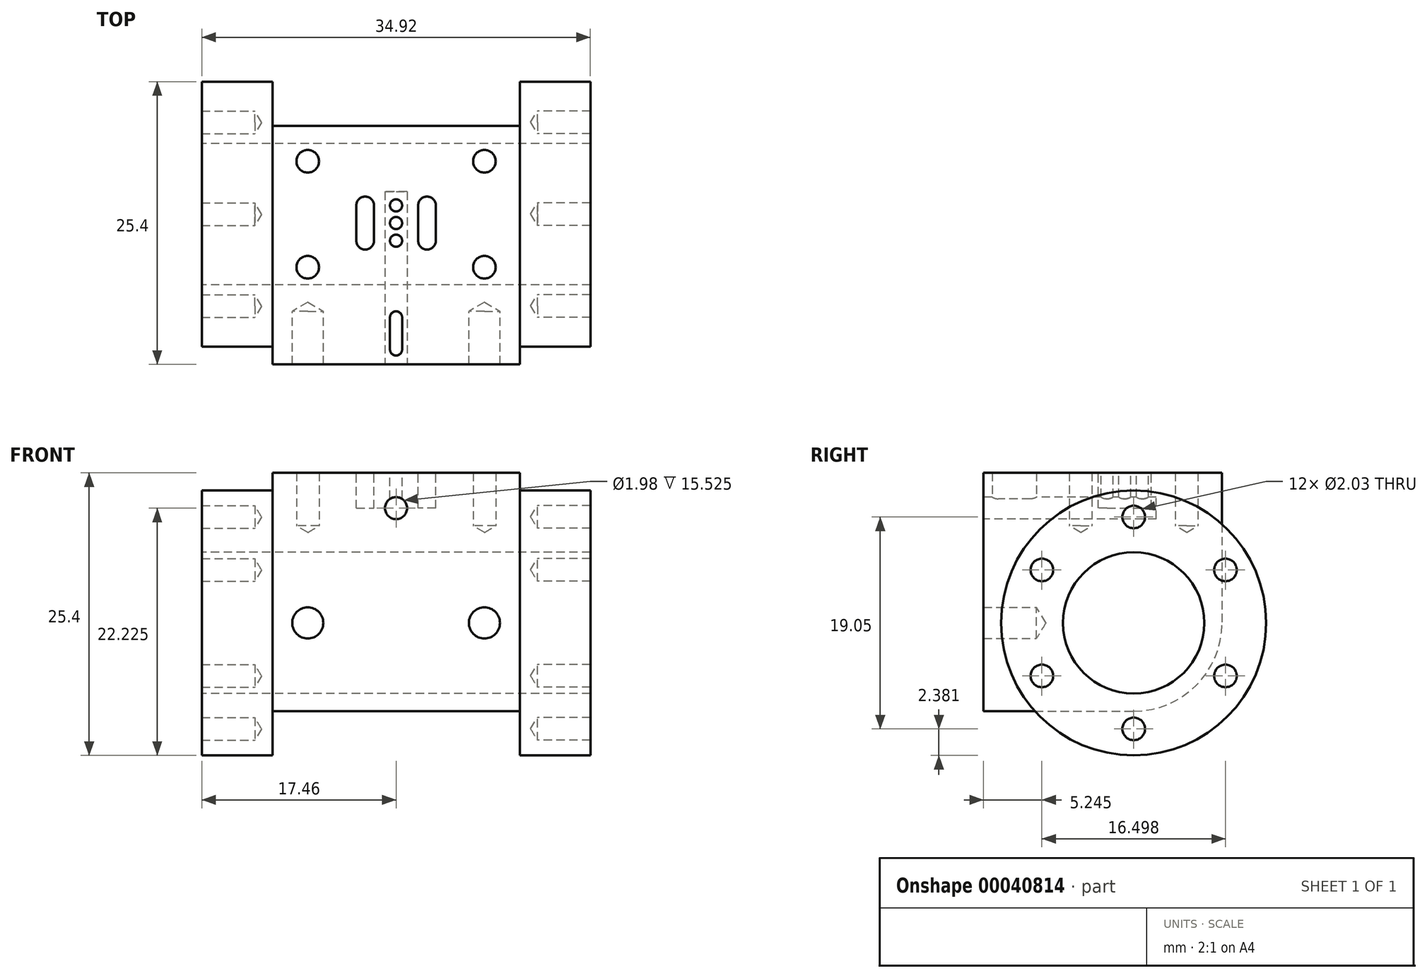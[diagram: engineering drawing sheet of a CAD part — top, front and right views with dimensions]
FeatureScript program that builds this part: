
annotation { "Feature Type Name" : "Feature", "Feature Type Description" : "" }
export const myFeature = defineFeature(function(context is Context, id is Id, definition is map)
    precondition{}
    {
        {
            var Q0;
            Q0=qCreatedBy(makeId("Top.planeOp"),FACE);
            var sketch = newSketch(context, id + "F0", { "sketchPlane" : qUnion([Q0])});
            skLineSegment(sketch, "E0.rect.bottom", {"start": v(-17.46, 12.7) * mm, "end": v(17.46, 12.7) * mm});
            skLineSegment(sketch, "E0.rect.top", {"start": v(-17.46, -12.7) * mm, "end": v(17.46, -12.7) * mm});
            skLineSegment(sketch, "E0.rect.left", {"start": v(-17.46, 12.7) * mm, "end": v(-17.46, -12.7) * mm});
            skLineSegment(sketch, "E0.rect.right", {"start": v(17.46, 12.7) * mm, "end": v(17.46, -12.7) * mm});
            skPoint(sketch, "E0.rect.middle", {"position": v(0, 0) * mm});
            skSolve(sketch);
        }
        {
            var Q0;
            Q0=makeQuery(id+"F0.imprint","IMPRINT",FACE,{"disambiguationData":[TD([[makeQuery(id+"F0.imprint","IMPRINT",EDGE,{"derivedFrom":sQuery(id+"F0.wireOp",EDGE,"E0.rect.bottom")}),-1.0]])]});
            extrude(context, id + "F1", {"entities" : qUnion([Q0]), "depth" : 25.4 * mm});
        }
        {
            var Q0;
            Q0=makeQuery(id+"F1.opExtrude","SWEPT_FACE",FACE,{"disambiguationData":[OSD([sQuery(id+"F0.wireOp",EDGE,"E0.rect.right")])]});
            var sketch = newSketch(context, id + "F2", { "sketchPlane" : qUnion([Q0])});
            skLineSegment(sketch, "E1.bottom", {"start": v(-12.7, 0) * mm, "end": v(12.7, 0) * mm});
            skLineSegment(sketch, "E1.top", {"start": v(-12.7, 25.4) * mm, "end": v(12.7, 25.4) * mm});
            skLineSegment(sketch, "E1.left", {"start": v(-12.7, 0) * mm, "end": v(-12.7, 25.4) * mm});
            skLineSegment(sketch, "E1.right", {"start": v(12.7, 0) * mm, "end": v(12.7, 25.4) * mm});
            skCircle(sketch, "E2", {"center": v(0.8, 11.9) * mm, "radius": 11.9 * mm});
            skSolve(sketch);
        }
        {
            var Q0;
            {var subQ6=sQuery(id+"F2.wireOp",EDGE,"E1.top");Q0=makeQuery(id+"F2.imprint","IMPRINT",FACE,{"disambiguationData":[TD([[makeQuery(id+"F2.imprint","IMPRINT",EDGE,{"derivedFrom":subQ6}),1.0]])]});}
            var Q1;
            {var subQ1=sQuery(id+"F2.wireOp",EDGE,"E1.right");var subQ3=sQuery(id+"F2.wireOp",EDGE,"E1.bottom");var subQ5=makeQuery(id+"F2.imprint","INTERSECT",VERTEX,{"derivedFrom":[subQ3,subQ1]});Q1=makeQuery(id+"F2.imprint","IMPRINT",FACE,{"disambiguationData":[TD([[makeQuery(id+"F2.imprint","IMPRINT",EDGE,{"disambiguationData":[TD([[subQ5,-1.0]])],"derivedFrom":subQ3}),-1.0]])]});}
            extrude(context, id + "F3", {"entities" : qUnion([Q0, Q1]), "operationType" : NewBodyOperationType.REMOVE, "oppositeDirection" : true, "depth" : 6.35 * mm});
        }
        {
            var Q0;
            Q0=makeQuery(id+"F1.opExtrude","SWEPT_FACE",FACE,{"disambiguationData":[OSD([sQuery(id+"F0.wireOp",EDGE,"E0.rect.left")])]});
            var sketch = newSketch(context, id + "F4", { "sketchPlane" : qUnion([Q0])});
            skLineSegment(sketch, "E3.bottom", {"start": v(-12.7, 0) * mm, "end": v(12.7, 0) * mm});
            skLineSegment(sketch, "E3.top", {"start": v(-12.7, 25.4) * mm, "end": v(12.7, 25.4) * mm});
            skLineSegment(sketch, "E3.left", {"start": v(-12.7, 0) * mm, "end": v(-12.7, 25.4) * mm});
            skLineSegment(sketch, "E3.right", {"start": v(12.7, 0) * mm, "end": v(12.7, 25.4) * mm});
            skCircle(sketch, "E4", {"center": v(-0.8, 11.9) * mm, "radius": 11.9 * mm});
            skSolve(sketch);
        }
        {
            var Q0;
            {var subQ6=sQuery(id+"F4.wireOp",EDGE,"E3.top");Q0=makeQuery(id+"F4.imprint","IMPRINT",FACE,{"disambiguationData":[TD([[makeQuery(id+"F4.imprint","IMPRINT",EDGE,{"derivedFrom":subQ6}),-1.0]])]});}
            var Q1;
            {var subQ1=sQuery(id+"F4.wireOp",EDGE,"E3.left");var subQ3=sQuery(id+"F4.wireOp",EDGE,"E3.bottom");var subQ5=makeQuery(id+"F4.imprint","INTERSECT",VERTEX,{"derivedFrom":[subQ3,subQ1]});Q1=makeQuery(id+"F4.imprint","IMPRINT",FACE,{"disambiguationData":[TD([[makeQuery(id+"F4.imprint","IMPRINT",EDGE,{"disambiguationData":[TD([[subQ5,-1.0]])],"derivedFrom":subQ3}),1.0]])]});}
            extrude(context, id + "F5", {"entities" : qUnion([Q0, Q1]), "operationType" : NewBodyOperationType.REMOVE, "oppositeDirection" : true, "depth" : 6.35 * mm});
        }
        {
            var Q0;
            Q0=sQuery(id+"F2.wireOp",VERTEX,"E2.center");
            var Q1;
            Q1=makeQuery(id+"F1.opExtrude","SWEPT_BODY",BODY,{"disambiguationData":[OSD([sQuery(id+"F0.wireOp",EDGE,"E0.rect.bottom"),sQuery(id+"F0.wireOp",EDGE,"E0.rect.top"),sQuery(id+"F0.wireOp",EDGE,"E0.rect.left"),sQuery(id+"F0.wireOp",EDGE,"E0.rect.right")])]});
            hole(context, id + "F6", {"style" : HoleStyle.SIMPLE, "holeDiameter" : 12.7 * mm, "endStyle" : HoleEndStyle.THROUGH, "locations" : qUnion([Q0]), "scope" : qUnion([Q1])});
        }
        {
            var Q0;
            Q0=makeQuery(id+"F3.boolean.opBoolean","COPY",FACE,{"derivedFrom":makeQuery(id+"F3.opExtrude","CAP_FACE",FACE,{"disambiguationData":[OSD([sQuery(id+"F2.wireOp",EDGE,"E1.bottom"),sQuery(id+"F2.wireOp",EDGE,"E1.top"),sQuery(id+"F2.wireOp",EDGE,"E1.left"),sQuery(id+"F2.wireOp",EDGE,"E1.right"),sQuery(id+"F2.wireOp",EDGE,"E2")])],"isStart":false})});
            cPlane(context, id + "F7", {"entities" : qUnion([Q0]), "cplaneType" : CPlaneType.OFFSET, "offset" : 0 * mm, "width" : 152.4 * mm, "height" : 152.4 * mm});
        }
        {
            var Q0;
            Q0=qCreatedBy(id+"F7.planeOp",FACE);
            var sketch = newSketch(context, id + "F8", { "sketchPlane" : qUnion([Q0])});
            skLineSegment(sketch, "E5.bottom", {"start": v(-12.7, 0) * mm, "end": v(12.7, 0) * mm});
            skLineSegment(sketch, "E5.top", {"start": v(-12.7, 25.4) * mm, "end": v(12.7, 25.4) * mm});
            skLineSegment(sketch, "E5.left", {"start": v(-12.7, 0) * mm, "end": v(-12.7, 25.4) * mm});
            skLineSegment(sketch, "E5.right", {"start": v(12.7, 0) * mm, "end": v(12.7, 25.4) * mm});
            skLineSegment(sketch, "E6", {"start": v(8.73, 25.4) * mm, "end": v(8.73, 11.9) * mm});
            skLineSegment(sketch, "E7", {"start": v(-12.7, 3.97) * mm, "end": v(0.8, 3.97) * mm});
            skArc(sketch, "E8", {"start": v(0.8, 3.97) * mm, "mid": v(6.4, 6.3) * mm, "end": v(8.73, 11.9) * mm});
            skSolve(sketch);
        }
        {
            var Q0;
            {var subQ2=sQuery(id+"F8.wireOp",EDGE,"E5.bottom");Q0=makeQuery(id+"F8.imprint","IMPRINT",FACE,{"disambiguationData":[TD([[makeQuery(id+"F8.imprint","IMPRINT",EDGE,{"derivedFrom":subQ2}),1.0]])]});}
            extrude(context, id + "F9", {"entities" : qUnion([Q0]), "operationType" : NewBodyOperationType.REMOVE, "oppositeDirection" : true, "depth" : 22.22 * mm});
        }
        {
            var Q0;
            Q0=makeQuery(id+"F1.opExtrude","SWEPT_FACE",FACE,{"disambiguationData":[OSD([sQuery(id+"F0.wireOp",EDGE,"E0.rect.top")])]});
            var sketch = newSketch(context, id + "F10", { "sketchPlane" : qUnion([Q0])});
            skLineSegment(sketch, "E9", {"start": v(-34.92, 11.9) * mm, "end": v(31.32, 11.9) * mm, "construction": true});
            skPoint(sketch, "E10", {"position": v(-7.94, 11.9) * mm});
            skPoint(sketch, "E11", {"position": v(7.94, 11.9) * mm});
            skSolve(sketch);
        }
        {
            var Q0;
            Q0=sQuery(id+"F10.wireOp",VERTEX,"E10");
            var Q1;
            Q1=sQuery(id+"F10.wireOp",VERTEX,"E11");
            var Q2;
            Q2=makeQuery(id+"F1.opExtrude","SWEPT_BODY",BODY,{"disambiguationData":[OSD([sQuery(id+"F0.wireOp",EDGE,"E0.rect.bottom"),sQuery(id+"F0.wireOp",EDGE,"E0.rect.top"),sQuery(id+"F0.wireOp",EDGE,"E0.rect.left"),sQuery(id+"F0.wireOp",EDGE,"E0.rect.right")])]});
            hole(context, id + "F11", {"style" : HoleStyle.SIMPLE, "holeDiameter" : 2.8 * mm, "endStyle" : HoleEndStyle.BLIND, "holeDepth" : 4.76 * mm, "locations" : qUnion([Q0, Q1]), "scope" : qUnion([Q2])});
        }
        {
            var Q0;
            Q0=makeQuery(id+"F1.opExtrude","CAP_FACE",FACE,{"disambiguationData":[OSD([sQuery(id+"F0.wireOp",EDGE,"E0.rect.bottom"),sQuery(id+"F0.wireOp",EDGE,"E0.rect.top"),sQuery(id+"F0.wireOp",EDGE,"E0.rect.left"),sQuery(id+"F0.wireOp",EDGE,"E0.rect.right")])],"isStart":false});
            var sketch = newSketch(context, id + "F12", { "sketchPlane" : qUnion([Q0])});
            skLineSegment(sketch, "E12", {"start": v(-33.77, 5.56) * mm, "end": v(38.74, 5.56) * mm, "construction": true});
            skLineSegment(sketch, "E13", {"start": v(-34.6, -3.97) * mm, "end": v(38.74, -3.97) * mm, "construction": true});
            skLineSegment(sketch, "E14", {"start": v(-7.94, 20.19) * mm, "end": v(-7.94, -25.42) * mm, "construction": true});
            skLineSegment(sketch, "E15", {"start": v(7.94, 21) * mm, "end": v(7.94, -27.26) * mm, "construction": true});
            skLineSegment(sketch, "E16", {"start": v(-62.53, 0.8) * mm, "end": v(55.18, 0.8) * mm, "construction": true});
            skPoint(sketch, "E17", {"position": v(-7.94, 5.56) * mm});
            skPoint(sketch, "E18", {"position": v(7.94, 5.56) * mm});
            skPoint(sketch, "E19", {"position": v(-7.94, -3.97) * mm});
            skPoint(sketch, "E20", {"position": v(7.94, -3.97) * mm});
            skSolve(sketch);
        }
        {
            var Q0;
            Q0=sQuery(id+"F12.wireOp",VERTEX,"E17");
            var Q1;
            Q1=sQuery(id+"F12.wireOp",VERTEX,"E18");
            var Q2;
            Q2=sQuery(id+"F12.wireOp",VERTEX,"E20");
            var Q3;
            Q3=sQuery(id+"F12.wireOp",VERTEX,"E19");
            var Q4;
            Q4=makeQuery(id+"F1.opExtrude","SWEPT_BODY",BODY,{"disambiguationData":[OSD([sQuery(id+"F0.wireOp",EDGE,"E0.rect.bottom"),sQuery(id+"F0.wireOp",EDGE,"E0.rect.top"),sQuery(id+"F0.wireOp",EDGE,"E0.rect.left"),sQuery(id+"F0.wireOp",EDGE,"E0.rect.right")])]});
            hole(context, id + "F13", {"style" : HoleStyle.SIMPLE, "holeDiameter" : 2.03 * mm, "endStyle" : HoleEndStyle.BLIND, "holeDepth" : 4.76 * mm, "locations" : qUnion([Q0, Q1, Q2, Q3]), "scope" : qUnion([Q4])});
        }
        {
            var Q0;
            Q0=makeQuery(id+"F1.opExtrude","SWEPT_FACE",FACE,{"disambiguationData":[OSD([sQuery(id+"F0.wireOp",EDGE,"E0.rect.right")])]});
            var sketch = newSketch(context, id + "F14", { "sketchPlane" : qUnion([Q0])});
            skLineSegment(sketch, "E21", {"start": v(0.8, 11.9) * mm, "end": v(0.8, 34.4) * mm, "construction": true});
            skPoint(sketch, "E22", {"position": v(0.8, 21.43) * mm});
            skPoint(sketch, "E23.1.0", {"position": v(9.04, 16.67) * mm});
            skPoint(sketch, "E23.2.0", {"position": v(9.04, 7.14) * mm});
            skPoint(sketch, "E23.3.0", {"position": v(0.8, 2.38) * mm});
            skPoint(sketch, "E23.4.0", {"position": v(-7.46, 7.14) * mm});
            skPoint(sketch, "E23.5.0", {"position": v(-7.46, 16.67) * mm});
            skPoint(sketch, "E23.center", {"position": v(0.8, 11.9) * mm});
            skLineSegment(sketch, "E23.anchor1", {"start": v(0.8, 11.9) * mm, "end": v(0.8, 21.43) * mm, "construction": true});
            skLineSegment(sketch, "E23.anchor2", {"start": v(0.8, 11.9) * mm, "end": v(-7.46, 16.67) * mm, "construction": true});
            skSolve(sketch);
        }
        {
            var Q0;
            Q0=makeQuery(id+"F1.opExtrude","SWEPT_FACE",FACE,{"disambiguationData":[OSD([sQuery(id+"F0.wireOp",EDGE,"E0.rect.left")])]});
            var sketch = newSketch(context, id + "F15", { "sketchPlane" : qUnion([Q0])});
            skLineSegment(sketch, "E24", {"start": v(-0.8, 11.9) * mm, "end": v(-0.8, 27.98) * mm, "construction": true});
            skPoint(sketch, "E25", {"position": v(-0.8, 21.43) * mm});
            skPoint(sketch, "E26.1.0", {"position": v(-9.04, 16.67) * mm});
            skPoint(sketch, "E26.2.0", {"position": v(-9.04, 7.14) * mm});
            skPoint(sketch, "E26.3.0", {"position": v(-0.8, 2.38) * mm});
            skPoint(sketch, "E26.4.0", {"position": v(7.46, 7.14) * mm});
            skPoint(sketch, "E26.5.0", {"position": v(7.46, 16.67) * mm});
            skPoint(sketch, "E26.center", {"position": v(-0.8, 11.9) * mm});
            skSolve(sketch);
        }
        {
            var Q0;
            Q0=sQuery(id+"F14.wireOp",VERTEX,"E22");
            var Q1;
            Q1=sQuery(id+"F14.wireOp",VERTEX,"E23.1.0");
            var Q2;
            Q2=sQuery(id+"F14.wireOp",VERTEX,"E23.2.0");
            var Q3;
            Q3=sQuery(id+"F14.wireOp",VERTEX,"E23.3.0");
            var Q4;
            Q4=sQuery(id+"F14.wireOp",VERTEX,"E23.4.0");
            var Q5;
            Q5=sQuery(id+"F14.wireOp",VERTEX,"E23.5.0");
            var Q6;
            Q6=sQuery(id+"F15.wireOp",VERTEX,"E25");
            var Q7;
            Q7=sQuery(id+"F15.wireOp",VERTEX,"E26.1.0");
            var Q8;
            Q8=sQuery(id+"F15.wireOp",VERTEX,"E26.2.0");
            var Q9;
            Q9=sQuery(id+"F15.wireOp",VERTEX,"E26.3.0");
            var Q10;
            Q10=sQuery(id+"F15.wireOp",VERTEX,"E26.4.0");
            var Q11;
            Q11=sQuery(id+"F15.wireOp",VERTEX,"E26.5.0");
            var Q12;
            Q12=makeQuery(id+"F1.opExtrude","SWEPT_BODY",BODY,{"disambiguationData":[OSD([sQuery(id+"F0.wireOp",EDGE,"E0.rect.bottom"),sQuery(id+"F0.wireOp",EDGE,"E0.rect.top"),sQuery(id+"F0.wireOp",EDGE,"E0.rect.left"),sQuery(id+"F0.wireOp",EDGE,"E0.rect.right")])]});
            hole(context, id + "F16", {"style" : HoleStyle.SIMPLE, "holeDiameter" : 2.03 * mm, "endStyle" : HoleEndStyle.BLIND, "holeDepth" : 4.76 * mm, "locations" : qUnion([Q0, Q1, Q2, Q3, Q4, Q5, Q6, Q7, Q8, Q9, Q10, Q11]), "scope" : qUnion([Q12])});
        }
        {
            var Q0;
            Q0=makeQuery(id+"F1.opExtrude","CAP_FACE",FACE,{"disambiguationData":[OSD([sQuery(id+"F0.wireOp",EDGE,"E0.rect.bottom"),sQuery(id+"F0.wireOp",EDGE,"E0.rect.top"),sQuery(id+"F0.wireOp",EDGE,"E0.rect.left"),sQuery(id+"F0.wireOp",EDGE,"E0.rect.right")])],"isStart":false});
            var sketch = newSketch(context, id + "F17", { "sketchPlane" : qUnion([Q0])});
            skLineSegment(sketch, "E27.rect.bottom", {"start": v(1.98, -2.38) * mm, "end": v(3.57, -2.38) * mm});
            skLineSegment(sketch, "E27.rect.top", {"start": v(1.98, 2.38) * mm, "end": v(3.57, 2.38) * mm});
            skLineSegment(sketch, "E27.rect.left", {"start": v(1.98, -2.38) * mm, "end": v(1.98, 2.38) * mm});
            skLineSegment(sketch, "E27.rect.right", {"start": v(3.57, -2.38) * mm, "end": v(3.57, 2.38) * mm});
            skPoint(sketch, "E27.rect.middle", {"position": v(2.78, 0) * mm});
            skLineSegment(sketch, "E28.rect.bottom", {"start": v(-1.98, -2.38) * mm, "end": v(-3.57, -2.38) * mm});
            skLineSegment(sketch, "E28.rect.top", {"start": v(-1.98, 2.38) * mm, "end": v(-3.57, 2.38) * mm});
            skLineSegment(sketch, "E28.rect.left", {"start": v(-1.98, -2.38) * mm, "end": v(-1.98, 2.38) * mm});
            skLineSegment(sketch, "E28.rect.right", {"start": v(-3.57, -2.38) * mm, "end": v(-3.57, 2.38) * mm});
            skPoint(sketch, "E28.rect.middle", {"position": v(-2.78, 0) * mm});
            skLineSegment(sketch, "E29", {"start": v(1.98, 0) * mm, "end": v(-1.98, 0) * mm, "construction": true});
            skPoint(sketch, "E30", {"position": v(0, 0) * mm});
            skSolve(sketch);
        }
        {
            var Q0;
            Q0 = qSketchRegion(id + "F17", true);
            extrude(context, id + "F18", {"entities" : qUnion([Q0]), "operationType" : NewBodyOperationType.REMOVE, "oppositeDirection" : true, "depth" : 3.17 * mm});
        }
        {
            var Q0;
            Q0=makeQuery(id+"F18.boolean.opBoolean","COPY",EDGE,{"derivedFrom":makeQuery(id+"F18.opExtrude","SWEPT_EDGE",EDGE,{"disambiguationData":[OSD([sQuery(id+"F17.wireOp",EDGE,"E28.rect.top"),sQuery(id+"F17.wireOp",EDGE,"E28.rect.right")])]})});
            var Q1;
            Q1=makeQuery(id+"F18.boolean.opBoolean","COPY",EDGE,{"derivedFrom":makeQuery(id+"F18.opExtrude","SWEPT_EDGE",EDGE,{"disambiguationData":[OSD([sQuery(id+"F17.wireOp",EDGE,"E28.rect.top"),sQuery(id+"F17.wireOp",EDGE,"E28.rect.left")])]})});
            var Q2;
            Q2=makeQuery(id+"F18.boolean.opBoolean","COPY",EDGE,{"derivedFrom":makeQuery(id+"F18.opExtrude","SWEPT_EDGE",EDGE,{"disambiguationData":[OSD([sQuery(id+"F17.wireOp",EDGE,"E28.rect.bottom"),sQuery(id+"F17.wireOp",EDGE,"E28.rect.left")])]})});
            var Q3;
            Q3=makeQuery(id+"F18.boolean.opBoolean","COPY",EDGE,{"derivedFrom":makeQuery(id+"F18.opExtrude","SWEPT_EDGE",EDGE,{"disambiguationData":[OSD([sQuery(id+"F17.wireOp",EDGE,"E28.rect.bottom"),sQuery(id+"F17.wireOp",EDGE,"E28.rect.right")])]})});
            var Q4;
            Q4=makeQuery(id+"F18.boolean.opBoolean","COPY",EDGE,{"derivedFrom":makeQuery(id+"F18.opExtrude","SWEPT_EDGE",EDGE,{"disambiguationData":[OSD([sQuery(id+"F17.wireOp",EDGE,"E27.rect.bottom"),sQuery(id+"F17.wireOp",EDGE,"E27.rect.left")])]})});
            var Q5;
            Q5=makeQuery(id+"F18.boolean.opBoolean","COPY",EDGE,{"derivedFrom":makeQuery(id+"F18.opExtrude","SWEPT_EDGE",EDGE,{"disambiguationData":[OSD([sQuery(id+"F17.wireOp",EDGE,"E27.rect.top"),sQuery(id+"F17.wireOp",EDGE,"E27.rect.right")])]})});
            var Q6;
            Q6=makeQuery(id+"F18.boolean.opBoolean","COPY",EDGE,{"derivedFrom":makeQuery(id+"F18.opExtrude","SWEPT_EDGE",EDGE,{"disambiguationData":[OSD([sQuery(id+"F17.wireOp",EDGE,"E27.rect.top"),sQuery(id+"F17.wireOp",EDGE,"E27.rect.left")])]})});
            var Q7;
            Q7=makeQuery(id+"F18.boolean.opBoolean","COPY",EDGE,{"derivedFrom":makeQuery(id+"F18.opExtrude","SWEPT_EDGE",EDGE,{"disambiguationData":[OSD([sQuery(id+"F17.wireOp",EDGE,"E27.rect.bottom"),sQuery(id+"F17.wireOp",EDGE,"E27.rect.right")])]})});
            fillet(context, id + "F19", {"entities" : qUnion([Q0, Q1, Q2, Q3, Q4, Q5, Q6, Q7]), "radius" : 0.8 * mm, "tangentPropagation" : true, "allowEdgeOverflow" : false});
        }
        {
            var Q0;
            Q0=makeQuery(id+"F1.opExtrude","SWEPT_FACE",FACE,{"disambiguationData":[OSD([sQuery(id+"F0.wireOp",EDGE,"E0.rect.top")])]});
            var sketch = newSketch(context, id + "F20", { "sketchPlane" : qUnion([Q0])});
            skCircle(sketch, "E31", {"center": v(0, 22.23) * mm, "radius": 1 * mm});
            skSolve(sketch);
        }
        {
            var Q0;
            Q0 = qSketchRegion(id + "F20", true);
            extrude(context, id + "F21", {"entities" : qUnion([Q0]), "operationType" : NewBodyOperationType.REMOVE, "oppositeDirection" : true, "depth" : 15.52 * mm});
        }
        {
            var Q0;
            Q0=makeQuery(id+"F1.opExtrude","CAP_FACE",FACE,{"disambiguationData":[OSD([sQuery(id+"F0.wireOp",EDGE,"E0.rect.bottom"),sQuery(id+"F0.wireOp",EDGE,"E0.rect.top"),sQuery(id+"F0.wireOp",EDGE,"E0.rect.left"),sQuery(id+"F0.wireOp",EDGE,"E0.rect.right")])],"isStart":false});
            var sketch = newSketch(context, id + "F22", { "sketchPlane" : qUnion([Q0])});
            skCircle(sketch, "E32", {"center": v(0, 0) * mm, "radius": 0.55 * mm});
            skCircle(sketch, "E33", {"center": v(0, 1.59) * mm, "radius": 0.55 * mm});
            skCircle(sketch, "E34", {"center": v(0, -1.59) * mm, "radius": 0.55 * mm});
            skLineSegment(sketch, "E35.rect.bottom", {"start": v(0.55, -7.94) * mm, "end": v(-0.55, -7.94) * mm});
            skLineSegment(sketch, "E35.rect.top", {"start": v(0.55, -11.9) * mm, "end": v(-0.55, -11.9) * mm});
            skLineSegment(sketch, "E35.rect.left", {"start": v(0.55, -7.94) * mm, "end": v(0.55, -11.9) * mm});
            skLineSegment(sketch, "E35.rect.right", {"start": v(-0.55, -7.94) * mm, "end": v(-0.55, -11.9) * mm});
            skPoint(sketch, "E35.rect.middle", {"position": v(0, -9.92) * mm});
            skSolve(sketch);
        }
        {
            var Q0;
            Q0 = qSketchRegion(id + "F22", true);
            extrude(context, id + "F23", {"entities" : qUnion([Q0]), "operationType" : NewBodyOperationType.REMOVE, "oppositeDirection" : true, "depth" : 3.17 * mm});
        }
        {
            var Q0;
            Q0=makeQuery(id+"F23.boolean.opBoolean","COPY",EDGE,{"derivedFrom":makeQuery(id+"F23.opExtrude","SWEPT_EDGE",EDGE,{"disambiguationData":[OSD([sQuery(id+"F22.wireOp",EDGE,"E35.rect.bottom"),sQuery(id+"F22.wireOp",EDGE,"E35.rect.right")])]})});
            var Q1;
            Q1=makeQuery(id+"F23.boolean.opBoolean","COPY",EDGE,{"derivedFrom":makeQuery(id+"F23.opExtrude","SWEPT_EDGE",EDGE,{"disambiguationData":[OSD([sQuery(id+"F22.wireOp",EDGE,"E35.rect.bottom"),sQuery(id+"F22.wireOp",EDGE,"E35.rect.left")])]})});
            var Q2;
            Q2=makeQuery(id+"F23.boolean.opBoolean","COPY",EDGE,{"derivedFrom":makeQuery(id+"F23.opExtrude","SWEPT_EDGE",EDGE,{"disambiguationData":[OSD([sQuery(id+"F22.wireOp",EDGE,"E35.rect.top"),sQuery(id+"F22.wireOp",EDGE,"E35.rect.left")])]})});
            var Q3;
            Q3=makeQuery(id+"F23.boolean.opBoolean","COPY",EDGE,{"derivedFrom":makeQuery(id+"F23.opExtrude","SWEPT_EDGE",EDGE,{"disambiguationData":[OSD([sQuery(id+"F22.wireOp",EDGE,"E35.rect.top"),sQuery(id+"F22.wireOp",EDGE,"E35.rect.right")])]})});
            fillet(context, id + "F24", {"entities" : qUnion([Q0, Q1, Q2, Q3]), "radius" : 0.55 * mm, "tangentPropagation" : true, "allowEdgeOverflow" : false});
        }
    });
